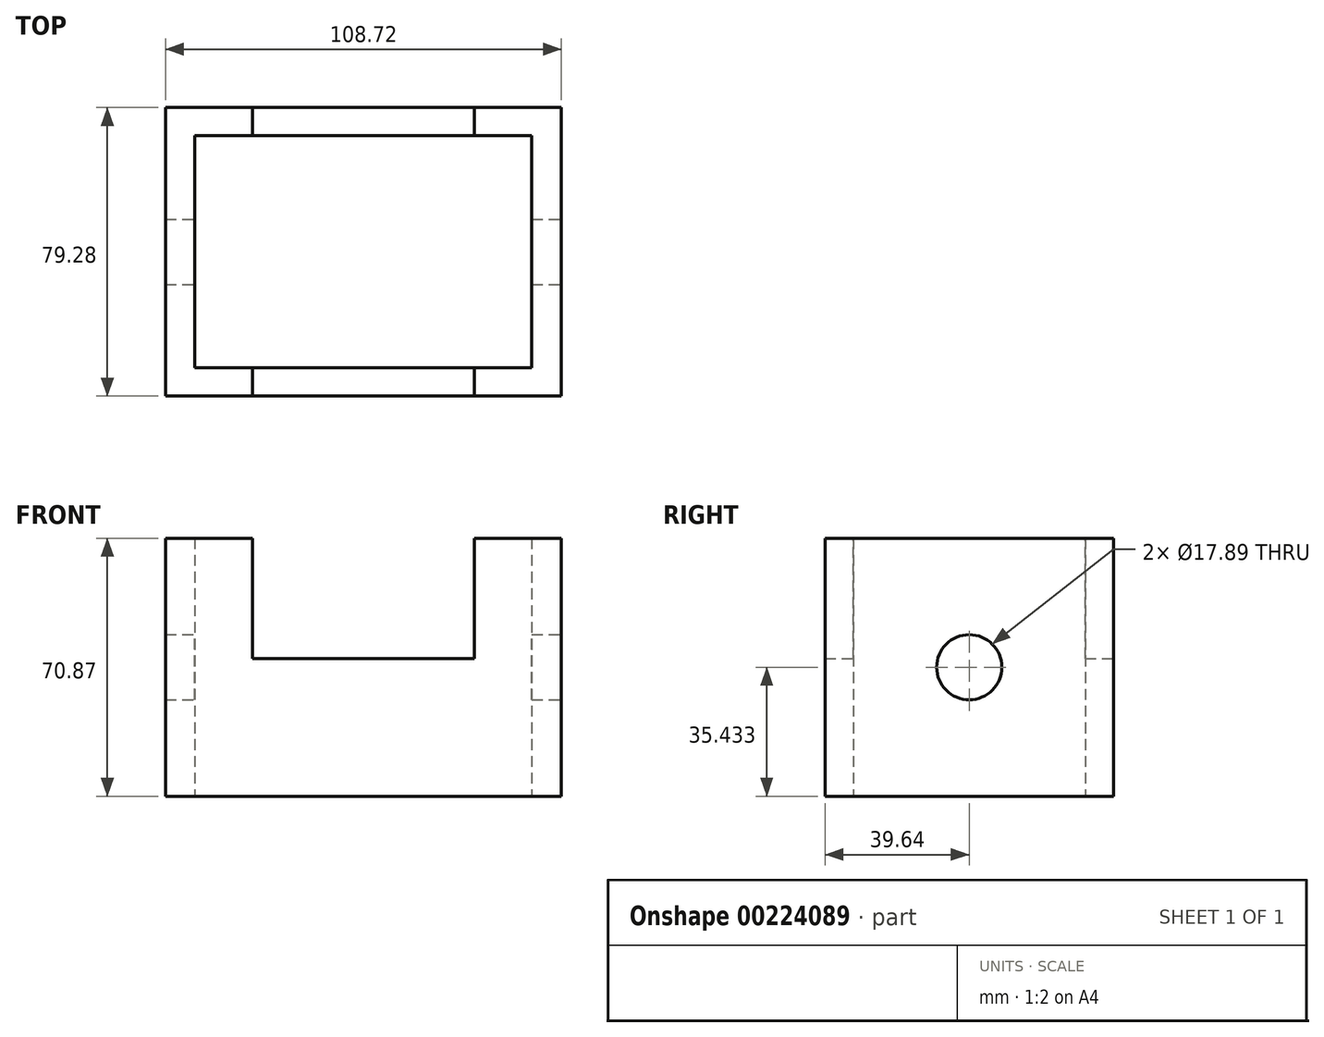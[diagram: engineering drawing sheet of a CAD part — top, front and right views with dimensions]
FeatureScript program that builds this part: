
annotation { "Feature Type Name" : "Feature", "Feature Type Description" : "" }
export const myFeature = defineFeature(function(context is Context, id is Id, definition is map)
    precondition{}
    {
        {
            var Q0;
            Q0=qCreatedBy(makeId("Top.planeOp"),FACE);
            var sketch = newSketch(context, id + "F0", { "sketchPlane" : qUnion([Q0])});
            skLineSegment(sketch, "E0.bottom", {"start": v(54.36, 39.64) * mm, "end": v(-54.36, 39.64) * mm});
            skLineSegment(sketch, "E0.top", {"start": v(54.36, -39.64) * mm, "end": v(-54.36, -39.64) * mm});
            skLineSegment(sketch, "E0.left", {"start": v(54.36, 39.64) * mm, "end": v(54.36, -39.64) * mm});
            skLineSegment(sketch, "E0.right", {"start": v(-54.36, 39.64) * mm, "end": v(-54.36, -39.64) * mm});
            skPoint(sketch, "E0.middle", {"position": v(0, 0) * mm});
            skLineSegment(sketch, "E1.bottom", {"start": v(46.28, 31.87) * mm, "end": v(-46.28, 31.87) * mm});
            skLineSegment(sketch, "E1.top", {"start": v(46.28, -31.87) * mm, "end": v(-46.28, -31.87) * mm});
            skLineSegment(sketch, "E1.left", {"start": v(46.28, 31.87) * mm, "end": v(46.28, -31.87) * mm});
            skLineSegment(sketch, "E1.right", {"start": v(-46.28, 31.87) * mm, "end": v(-46.28, -31.87) * mm});
            skSolve(sketch);
        }
        {
            var Q0;
            Q0=makeQuery(id+"F0.imprint","IMPRINT",FACE,{"disambiguationData":[TD([[makeQuery(id+"F0.imprint","IMPRINT",EDGE,{"derivedFrom":sQuery(id+"F0.wireOp",EDGE,"E0.bottom")}),1.0]])]});
            extrude(context, id + "F1", {"entities" : qUnion([Q0]), "depth" : 70.87 * mm});
        }
        {
            var Q0;
            Q0=makeQuery(id+"F1.opExtrude","SWEPT_FACE",FACE,{"disambiguationData":[OSD([sQuery(id+"F0.wireOp",EDGE,"E0.left")])]});
            var sketch = newSketch(context, id + "F2", { "sketchPlane" : qUnion([Q0])});
            skCircle(sketch, "E2", {"center": v(0, 35.43) * mm, "radius": 8.95 * mm});
            skSolve(sketch);
        }
        {
            var Q0;
            Q0 = qSketchRegion(id + "F2", true);
            extrude(context, id + "F3", {"entities" : qUnion([Q0]), "operationType" : NewBodyOperationType.REMOVE, "oppositeDirection" : true, "depth" : 254 * mm});
        }
        {
            var Q0;
            Q0=makeQuery(id+"F1.opExtrude","SWEPT_FACE",FACE,{"disambiguationData":[OSD([sQuery(id+"F0.wireOp",EDGE,"E0.bottom")])]});
            var sketch = newSketch(context, id + "F4", { "sketchPlane" : qUnion([Q0])});
            skLineSegment(sketch, "E3", {"start": v(0, 70.87) * mm, "end": v(-30.48, 70.87) * mm});
            skLineSegment(sketch, "E4", {"start": v(-30.48, 70.87) * mm, "end": v(-30.48, 37.85) * mm});
            skLineSegment(sketch, "E5", {"start": v(-30.48, 37.85) * mm, "end": v(30.48, 37.85) * mm});
            skLineSegment(sketch, "E6", {"start": v(30.48, 37.85) * mm, "end": v(30.48, 70.87) * mm});
            skLineSegment(sketch, "E7", {"start": v(30.48, 70.87) * mm, "end": v(0, 70.87) * mm});
            skSolve(sketch);
        }
        {
            var Q0;
            Q0 = qSketchRegion(id + "F4", true);
            extrude(context, id + "F5", {"entities" : qUnion([Q0]), "operationType" : NewBodyOperationType.REMOVE, "oppositeDirection" : true, "depth" : 254 * mm});
        }
    });
